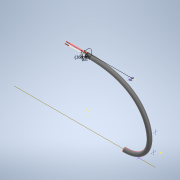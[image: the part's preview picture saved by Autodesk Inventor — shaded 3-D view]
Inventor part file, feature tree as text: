
AUTODESK INVENTOR PART (.ipt)
format: ipt  version: 2021 (Build 250183000, 183)  size: 218,112 bytes
history: native  units: mm
features: other x14, sketch x8, extrude x2, reference x2, sweep x1
ambient origin geometry x8: Origin, YZ Plane, XZ Plane, XY Plane, X Axis, Y Axis, Z Axis, Center Point
bodies: Body1 (feature_tree)
feature tree (27):
  other  "Bryła1"
  other  "Płaszczyzna konstrukcyjna1"
  sketch  "Szkic1"
  sketch  "Szkic 3D1"
  other  "Oś konstrukcyjna1"
  other  "Płaszczyzna konstrukcyjna4"
  sketch  "Szkic3"
  other  "Płaszczyzna konstrukcyjna5"
  other  "Płaszczyzna konstrukcyjna7"
  other  "Płaszczyzna konstrukcyjna8"
  other  "Płaszczyzna konstrukcyjna9"
  sketch  "Szkic5"
  sketch  "Szkic6"
  sketch  "Szkic 3D3"
  other  "Płaszczyzna konstrukcyjna11"
  sweep  "Przeciągnięcie1"
  sketch  "Szkic8"
  extrude  "Wyciągnięcie proste1"  Depth=2.5mm
  extrude  "Wyciągnięcie proste2"  Depth=2.0mm
  reference  "Odniesienie1"
  other  "Płaszczyzna konstrukcyjna10"
  sketch  "Szkic7"
  reference  "Odniesienie4"
  parser-record x1  (decoder bookkeeping rows leaked as tree rows — omitted from the tree; the rows remain in map.json)
  other  "model tensometru.iam"
  other  "kabelki:1"
  other  "podstwa:1"
note: 1 file-system path scrubbed to <path> (originals preserved in map.json)
